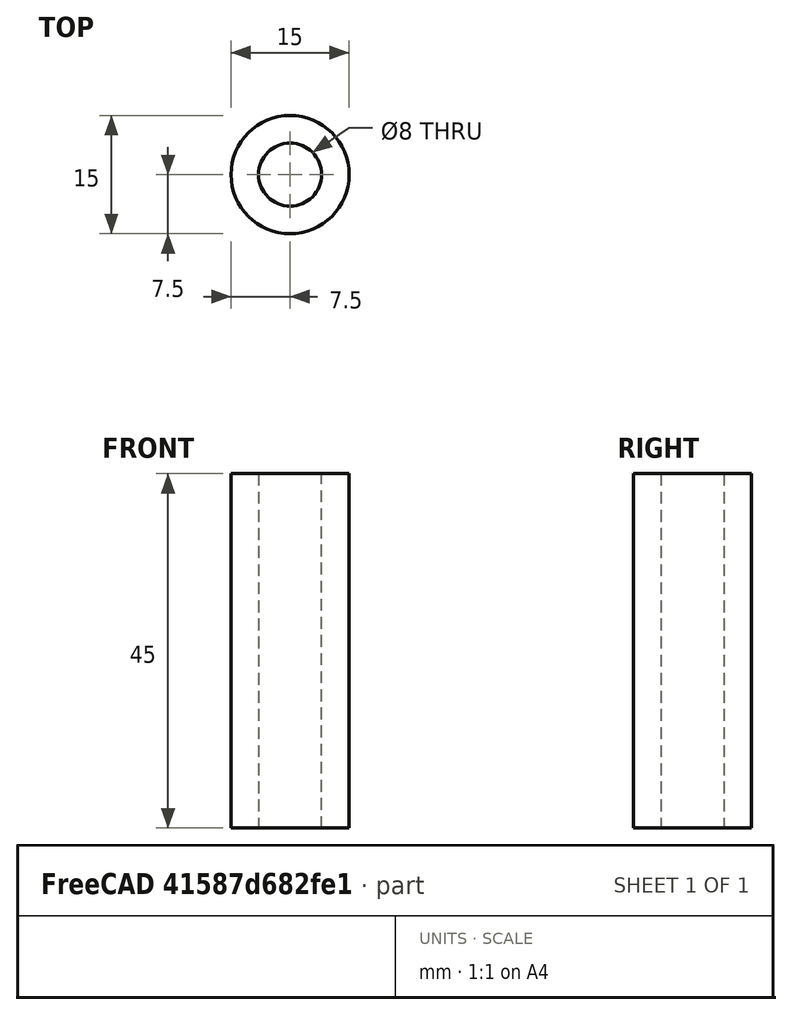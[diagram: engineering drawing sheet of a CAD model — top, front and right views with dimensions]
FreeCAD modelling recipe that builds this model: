
FCSTD DOCUMENT  (FreeCAD 0.18R14555 (Git shallow))
Label: round-bearing
License: All rights reserved
LicenseURL: http://en.wikipedia.org/wiki/All_rights_reserved
objects: Sketcher::SketchObject×1, PartDesign::Pad×1, PartDesign::Body×1
note: 4 computed .brp shape members not serialized (recipe doc carries the construction recipe); baked Part::Feature solids carry a one-line shape summary decoded from their .brp

FEATURE [Sketcher::SketchObject] Sketch
  MapMode = 5
  Support = -> [XY_Plane]
  sketch-geometry (2):
    g0: Circle CenterX=0 CenterY=0 CenterZ=0 NormalX=0 NormalY=0 NormalZ=1 AngleXU=0 Radius=4
    g1: Circle CenterX=0 CenterY=0 CenterZ=0 NormalX=0 NormalY=0 NormalZ=1 AngleXU=0 Radius=7.5
  constraints (4):
    c: Coincident(g0,g-1)
    c: Coincident(g1,g0)
    c: Radius(g0) = 4
    c: Radius(g1) = 7.5
FEATURE [PartDesign::Pad] Pad
  Length = 45
  Length2 = 100
  Profile = -> Sketch
  Type = 0
FEATURE [PartDesign::Body] Body
  Group = -> [Sketch,Pad]
  Origin = -> Origin
  Tip = -> Pad
